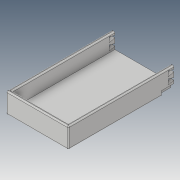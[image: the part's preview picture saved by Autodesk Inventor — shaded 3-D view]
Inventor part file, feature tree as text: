
AUTODESK INVENTOR PART (.ipt)
format: ipt  version: 2019 (Build 230136000, 136)  size: 172,544 bytes
history: native  units: mm
features: extrude x4, sketch x4, projected_geometry x2, fillet x1
ambient origin geometry x8: Origin, YZ Plane, XZ Plane, XY Plane, X Axis, Y Axis, Z Axis, Center Point
bodies: Solid1 (feature_tree)
feature tree (11):
  extrude  "Extrusion1"  Depth=150.0mm
  extrude  "Extrusion2"  Depth=5.0mm
  extrude  "Extrusion3"  Depth=25.0mm TaperAngle=0.0deg
  extrude  "Extrusion4"  Depth=3.0mm
  fillet  "Fillet1"  Radius=20.0mm
  sketch  "Sketch1"  dims[d0=100.0mm d1=150.0mm]
  sketch  "Sketch3"  dims[d2=8.0mm d3=0.0mm d4=5.0mm]
  projected_geometry  "Projected Loop2"
  sketch  "Sketch4"  dims[d5=5.0mm d6=25.0mm d7=0.0mm]
  projected_geometry  "Projected Loop3"
  sketch  "Sketch6"  dims[d8=3.0mm d9=3.0mm d10=20.0mm d11=0.0mm d14=3.5mm d15=9.0mm d16=2.5mm d17=2.5mm d18=3.5mm d19=2.5mm d20=2.0mm d21=8.0mm d22=9.0mm d23=20.0mm d24=0.0mm d25=2.0mm]
